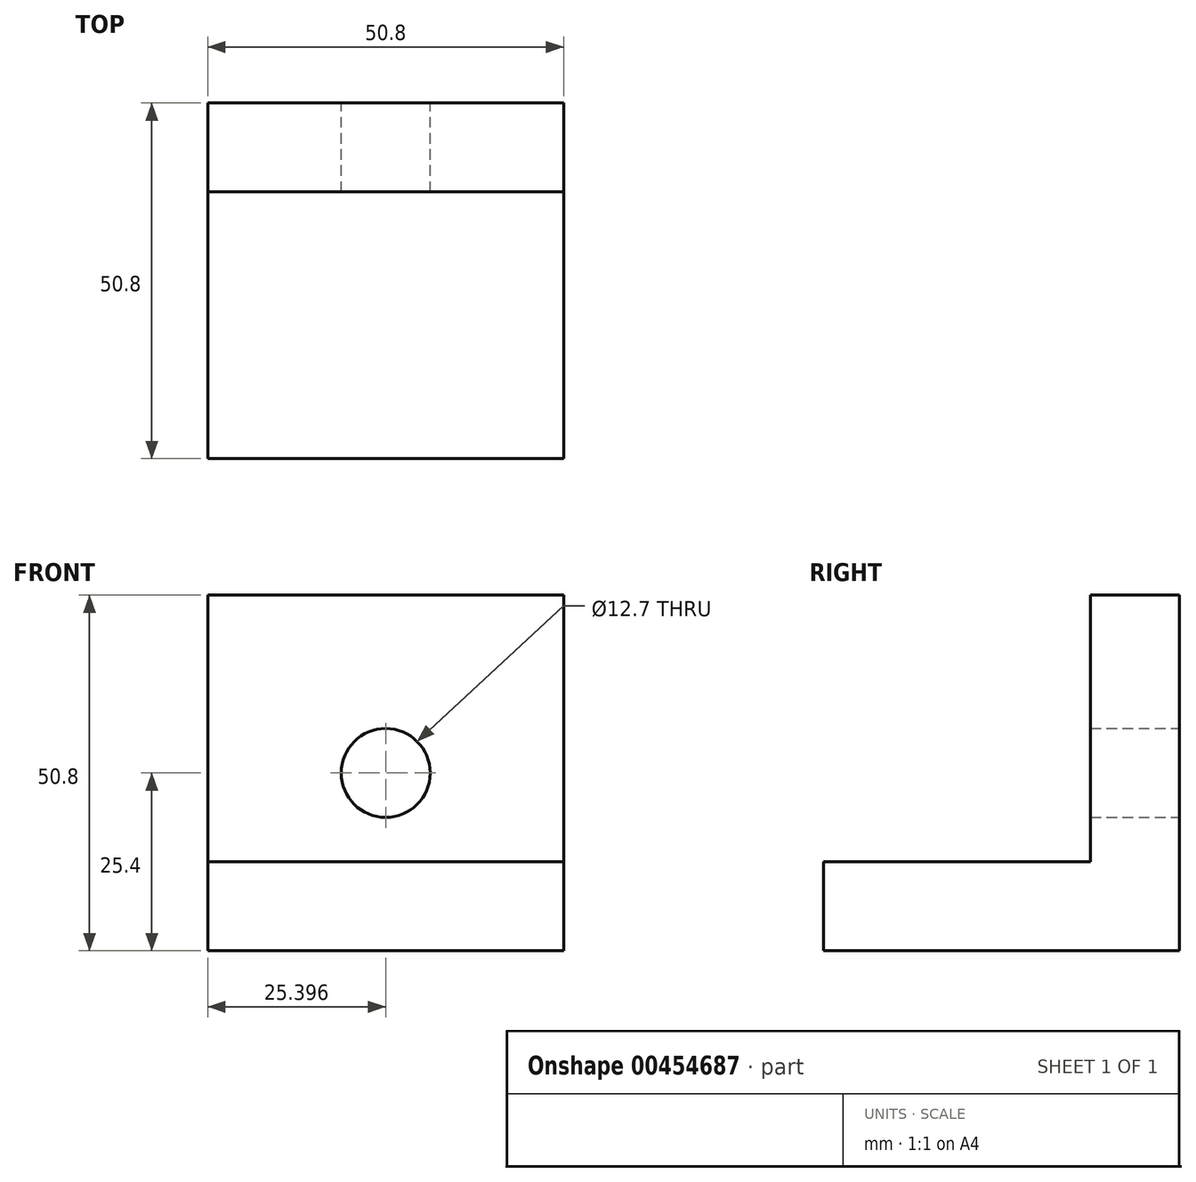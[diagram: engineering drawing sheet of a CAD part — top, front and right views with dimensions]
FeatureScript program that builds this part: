
annotation { "Feature Type Name" : "Feature", "Feature Type Description" : "" }
export const myFeature = defineFeature(function(context is Context, id is Id, definition is map)
    precondition{}
    {
        {
            var Q0;
            Q0=qCreatedBy(makeId("Front.planeOp"),FACE);
            var sketch = newSketch(context, id + "F0", { "sketchPlane" : qUnion([Q0])});
            skLineSegment(sketch, "E0.bottom", {"start": v(-31.13, -26.29) * mm, "end": v(19.67, -26.29) * mm});
            skLineSegment(sketch, "E0.top", {"start": v(-31.13, 24.51) * mm, "end": v(19.67, 24.51) * mm});
            skLineSegment(sketch, "E0.left", {"start": v(-31.13, -26.29) * mm, "end": v(-31.13, 24.51) * mm});
            skLineSegment(sketch, "E0.right", {"start": v(19.67, -26.29) * mm, "end": v(19.67, 24.51) * mm});
            skCircle(sketch, "E1", {"center": v(-5.73, -0.89) * mm, "radius": 6.35 * mm});
            skSolve(sketch);
        }
        {
            var Q0;
            Q0 = qSketchRegion(id + "F0", true);
            extrude(context, id + "F1", {"entities" : qUnion([Q0]), "depth" : 12.7 * mm});
        }
        {
            var Q0;
            Q0=makeQuery(id+"F1.opExtrude","CAP_FACE",FACE,{"disambiguationData":[OSD([sQuery(id+"F0.wireOp",EDGE,"E0.bottom"),sQuery(id+"F0.wireOp",EDGE,"E0.top"),sQuery(id+"F0.wireOp",EDGE,"E0.left"),sQuery(id+"F0.wireOp",EDGE,"E0.right"),sQuery(id+"F0.wireOp",EDGE,"E1")])],"isStart":false});
            var sketch = newSketch(context, id + "F2", { "sketchPlane" : qUnion([Q0])});
            skLineSegment(sketch, "E2.bottom", {"start": v(-31.13, -26.29) * mm, "end": v(19.67, -26.29) * mm});
            skLineSegment(sketch, "E2.top", {"start": v(-31.13, -13.59) * mm, "end": v(19.67, -13.59) * mm});
            skLineSegment(sketch, "E2.left", {"start": v(-31.13, -26.29) * mm, "end": v(-31.13, -13.59) * mm});
            skLineSegment(sketch, "E2.right", {"start": v(19.67, -26.29) * mm, "end": v(19.67, -13.59) * mm});
            skSolve(sketch);
        }
        {
            var Q0;
            Q0 = qSketchRegion(id + "F2", true);
            extrude(context, id + "F3", {"entities" : qUnion([Q0]), "operationType" : NewBodyOperationType.ADD, "depth" : 38.1 * mm});
        }
    });
